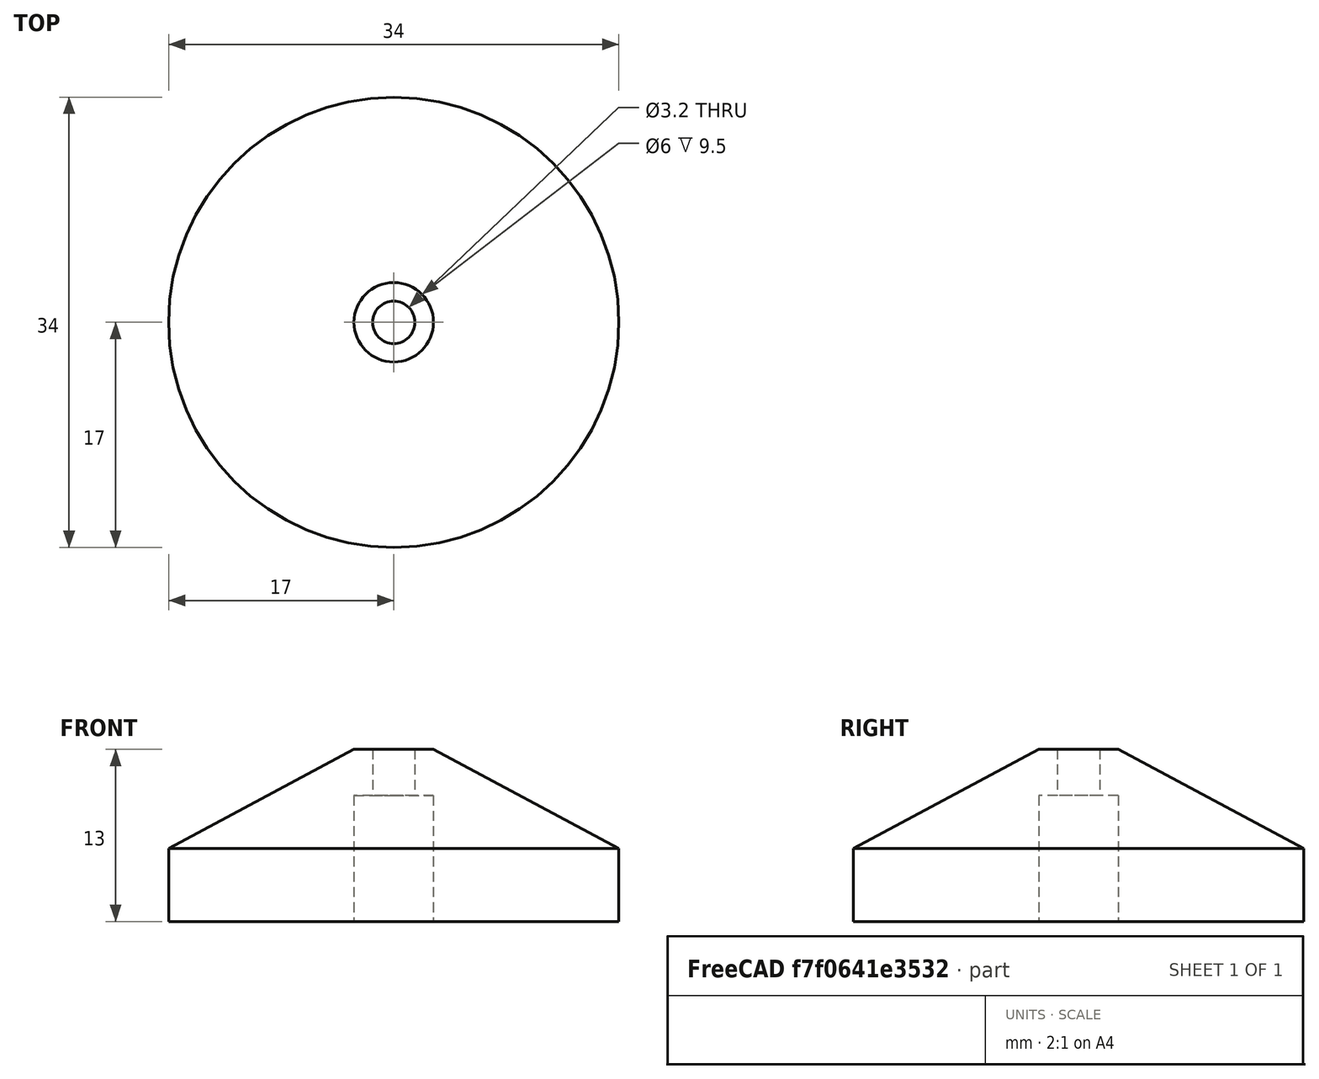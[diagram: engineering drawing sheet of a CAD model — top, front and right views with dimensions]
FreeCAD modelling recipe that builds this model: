
FCSTD DOCUMENT  (FreeCAD 0.16R6700 (Git))
Label: BobbinSocket_R_A1
License: All rights reserved
LicenseURL: http://en.wikipedia.org/wiki/All_rights_reserved
objects: Sketcher::SketchObject×1, PartDesign::Revolution×1
note: 3 computed .brp shape members not serialized (recipe doc carries the construction recipe); baked Part::Feature solids carry a one-line shape summary decoded from their .brp

FEATURE [Sketcher::SketchObject] Sketch002
  Placement = pos=(0,0,0) rot=(0.57735,0.57735,0.57735;2.0944rad)
  sketch-geometry (7):
    g0: LineSegment StartX=1.6 StartY=13 StartZ=0 EndX=1.6 EndY=9.5 EndZ=0
    g1: LineSegment StartX=17 StartY=0 StartZ=0 EndX=17 EndY=5.5 EndZ=0
    g2: LineSegment StartX=1.6 StartY=9.5 StartZ=0 EndX=3 EndY=9.5 EndZ=0
    g3: LineSegment StartX=3 StartY=9.5 StartZ=0 EndX=3 EndY=0 EndZ=0
    g4: LineSegment StartX=3 StartY=0 StartZ=0 EndX=17 EndY=0 EndZ=0
    g5: LineSegment StartX=1.6 StartY=13 StartZ=0 EndX=3 EndY=13 EndZ=0
    g6: LineSegment StartX=3 StartY=13 StartZ=0 EndX=17 EndY=5.5 EndZ=0
  constraints (21):
    c: PointOnObject(g1,g-1)
    c: Vertical(g1)
    c: DistanceX(g-1,g0) = 1.6
    c: Vertical(g0)
    c: Coincident(g0,g2)
    c: Coincident(g2,g3)
    c: PointOnObject(g3,g-1)
    c: Vertical(g3)
    c: Coincident(g3,g4)
    c: Coincident(g4,g1)
    c: DistanceX(g-1,g3) = 3
    c: DistanceY(g1,g1) = 5.5
    c: DistanceY(g-1,g0) = 13
    c: DistanceX(g-1,g1) = 17
    c: Horizontal(g2)
    c: DistanceY(g-1,g0) = 9.5
    c: Coincident(g0,g5)
    c: Horizontal(g5)
    c: Coincident(g5,g6)
    c: Coincident(g6,g1)
    c: DistanceX(g-1,g5) = 3
FEATURE [PartDesign::Revolution] Revolution
  Angle = 360
  Axis = (0,0,1)
  Base = (0,0,0)
  Placement = pos=(0,0,0) rot=(0.57735,0.57735,0.57735;2.0944rad)
  ReferenceAxis = -> Sketch002 [V_Axis]
  Reversed = true
  Sketch = -> Sketch002
